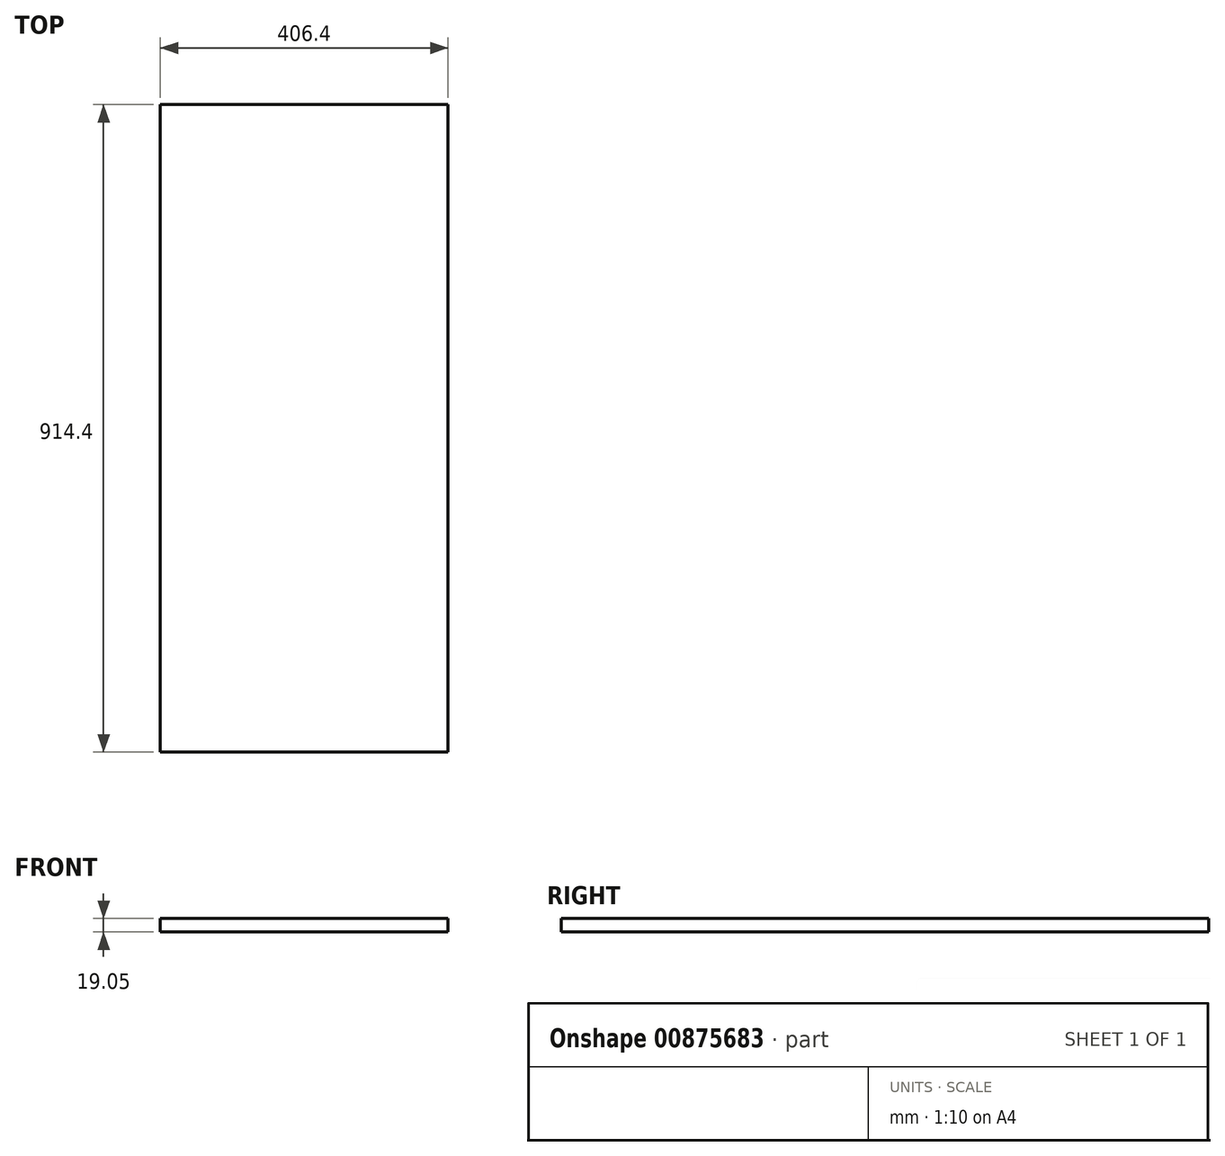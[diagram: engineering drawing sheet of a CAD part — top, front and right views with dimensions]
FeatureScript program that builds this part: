
annotation { "Feature Type Name" : "Feature", "Feature Type Description" : "" }
export const myFeature = defineFeature(function(context is Context, id is Id, definition is map)
    precondition{}
    {
        {
            var Q0;
            Q0=qCreatedBy(makeId("Top.planeOp"),FACE);
            var sketch = newSketch(context, id + "F0", { "sketchPlane" : qUnion([Q0])});
            skLineSegment(sketch, "E0.bottom", {"start": v(0, 914.4) * mm, "end": v(406.4, 914.4) * mm});
            skLineSegment(sketch, "E0.top", {"start": v(0, 0) * mm, "end": v(406.4, 0) * mm});
            skLineSegment(sketch, "E0.left", {"start": v(0, 914.4) * mm, "end": v(0, 0) * mm});
            skLineSegment(sketch, "E0.right", {"start": v(406.4, 914.4) * mm, "end": v(406.4, 0) * mm});
            skSolve(sketch);
        }
        {
            var Q0;
            Q0 = qSketchRegion(id + "F0", true);
            extrude(context, id + "F1", {"entities" : qUnion([Q0]), "depth" : 19.05 * mm, "offsetDistance" : 25.4 * mm});
        }
    });
